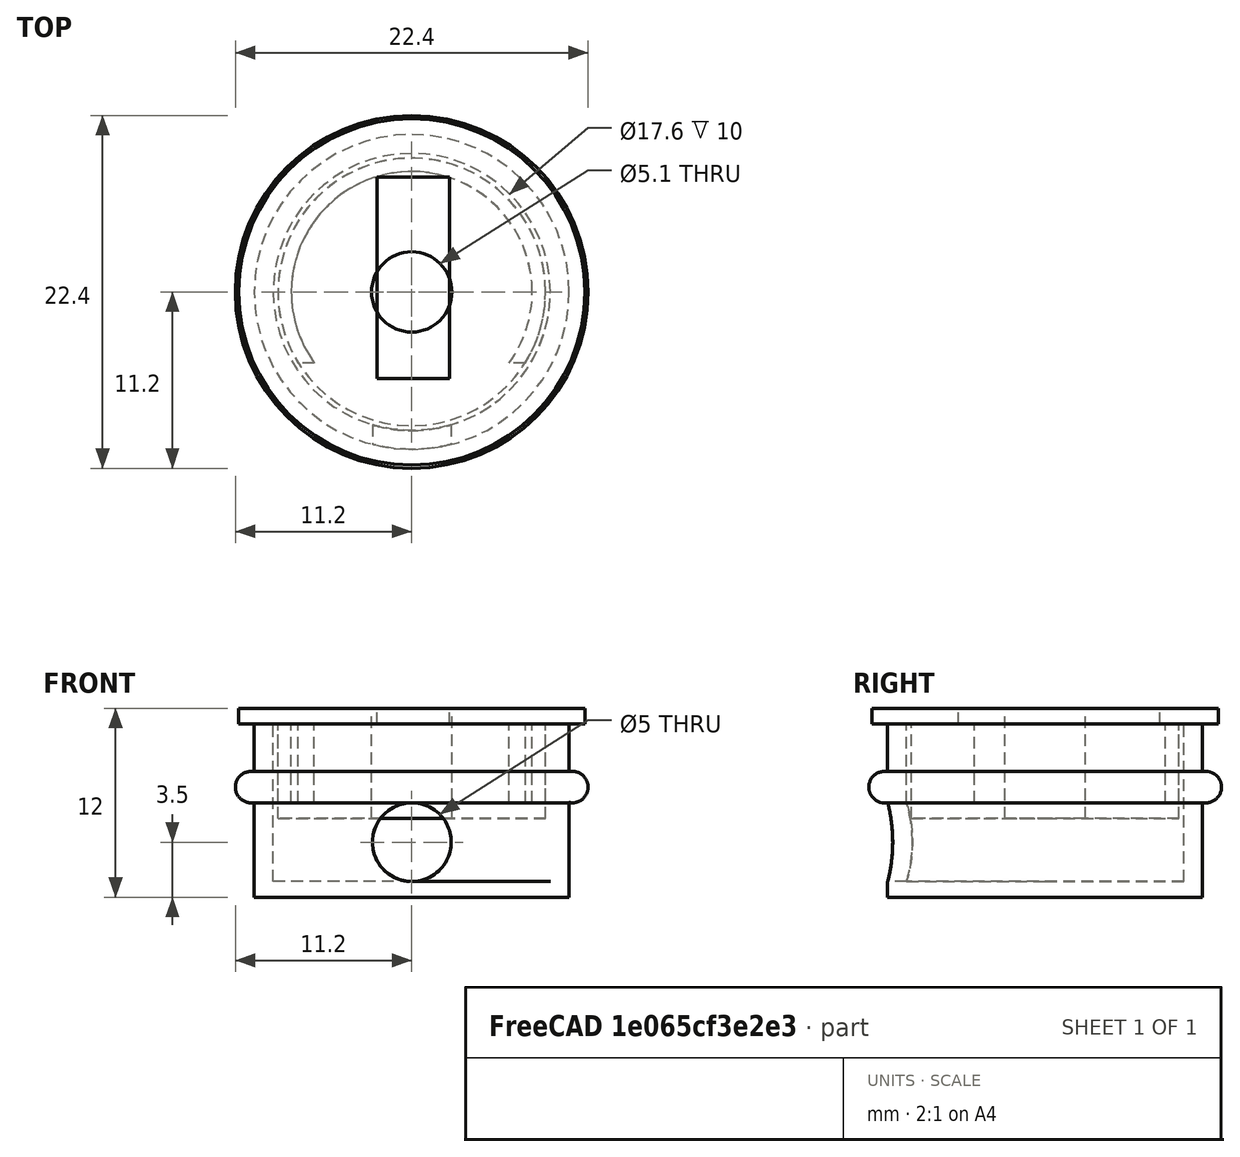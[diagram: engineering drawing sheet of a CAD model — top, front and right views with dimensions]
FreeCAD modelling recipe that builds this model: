
FCSTD DOCUMENT  (FreeCAD 0.17R13541 (Git))
Label: ir-schody_v2
License: All rights reserved
LicenseURL: http://en.wikipedia.org/wiki/All_rights_reserved
objects: Part::Cylinder×9, Part::Cut×5, Part::Fuse×4, Part::Box×2, Part::Torus×1
note: 21 computed .brp shape members not serialized (recipe doc carries the construction recipe); baked Part::Feature solids carry a one-line shape summary decoded from their .brp

FEATURE [Part::Cylinder] Cylinder  label="vnitrk-boxu"
  Angle = 360
  AttacherType = Attacher::AttachEngine3D
  Height = 10
  Radius = 8.8
FEATURE [Part::Cylinder] Cylinder001  label="vnejsek-boxu"
  Angle = 360
  AttacherType = Attacher::AttachEngine3D
  Height = 11
  Placement = pos=(0,0,-1) rot=(0,0,1;0rad)
  Radius = 10
FEATURE [Part::Cylinder] Cylinder002  label="Cylinder"
  Angle = 360
  AttacherType = Attacher::AttachEngine3D
  Height = 10
  Placement = pos=(0,0,2.5) rot=(1,0,0;1.5708rad)
  Radius = 2.5
FEATURE [Part::Fuse] Fusion
  Base = -> Cylinder
  Tool = -> Cylinder002
FEATURE [Part::Cut] Cut
  Base = -> Cylinder001
  Tool = -> Fusion
FEATURE [Part::Torus] Torus
  Angle1 = -180
  Angle2 = 180
  Angle3 = 360
  AttacherType = Attacher::AttachEngine3D
  Placement = pos=(0,0,6) rot=(0,0,1;0rad)
  Radius1 = 10.2
  Radius2 = 1
FEATURE [Part::Fuse] Fusion001  label="ir-box"
  Base = -> Cut
  Tool = -> Torus
FEATURE [Part::Cylinder] Cylinder003  label="zaklad-vnejsi"
  Angle = 360
  AttacherType = Attacher::AttachEngine3D
  Height = 6
  Placement = pos=(0,0,4) rot=(0,0,1;0rad)
  Radius = 8.5
FEATURE [Part::Cylinder] Cylinder004  label="zaklad-vnitrni"
  Angle = 360
  AttacherType = Attacher::AttachEngine3D
  Height = 12
  Placement = pos=(0,0,4) rot=(0,0,1;0rad)
  Radius = 2.55
FEATURE [Part::Cylinder] Cylinder005  label="zaklda-poklop"
  Angle = 360
  AttacherType = Attacher::AttachEngine3D
  Height = 1
  Placement = pos=(0,0,10) rot=(0,0,1;0rad)
  Radius = 11
FEATURE [Part::Fuse] Fusion002
  Base = -> Cylinder003
  Tool = -> Cylinder005
FEATURE [Part::Cut] Cut001  label="ir-sender"
  Base = -> Fusion002
  Tool = -> Cylinder004
FEATURE [Part::Cylinder] Cylinder006  label="Cylinder001"
  Angle = 360
  AttacherType = Attacher::AttachEngine3D
  Height = 5
  Placement = pos=(0,0,5) rot=(0,0,1;0rad)
  Radius = 8.5
FEATURE [Part::Cylinder] Cylinder007  label="Cylinder002"
  Angle = 360
  AttacherType = Attacher::AttachEngine3D
  Height = 5
  Placement = pos=(0,0,5) rot=(0,0,1;0rad)
  Radius = 7.65
FEATURE [Part::Cut] Cut002
  Base = -> Cylinder006
  Tool = -> Cylinder007
FEATURE [Part::Box] Box  label="Cube"
  AttacherType = Attacher::AttachEngine3D
  Height = 7
  Length = 18
  Placement = pos=(-9,-11.5,4) rot=(0,0,1;0rad)
  Width = 7
FEATURE [Part::Cut] Cut003
  Base = -> Cut002
  Tool = -> Box
FEATURE [Part::Cylinder] Cylinder008  label="zaklda-poklop001"
  Angle = 360
  AttacherType = Attacher::AttachEngine3D
  Height = 1
  Placement = pos=(0,0,10) rot=(0,0,1;0rad)
  Radius = 11
FEATURE [Part::Fuse] Fusion003
  Base = -> Cut003
  Tool = -> Cylinder008
FEATURE [Part::Box] Box001  label="Cube001"
  AttacherType = Attacher::AttachEngine3D
  Height = 3
  Length = 4.6
  Placement = pos=(-2.2,-5.5,10) rot=(0,0,1;0rad)
  Width = 12.8
FEATURE [Part::Cut] Cut004  label="ir-receiver"
  Base = -> Fusion003
  Tool = -> Box001
